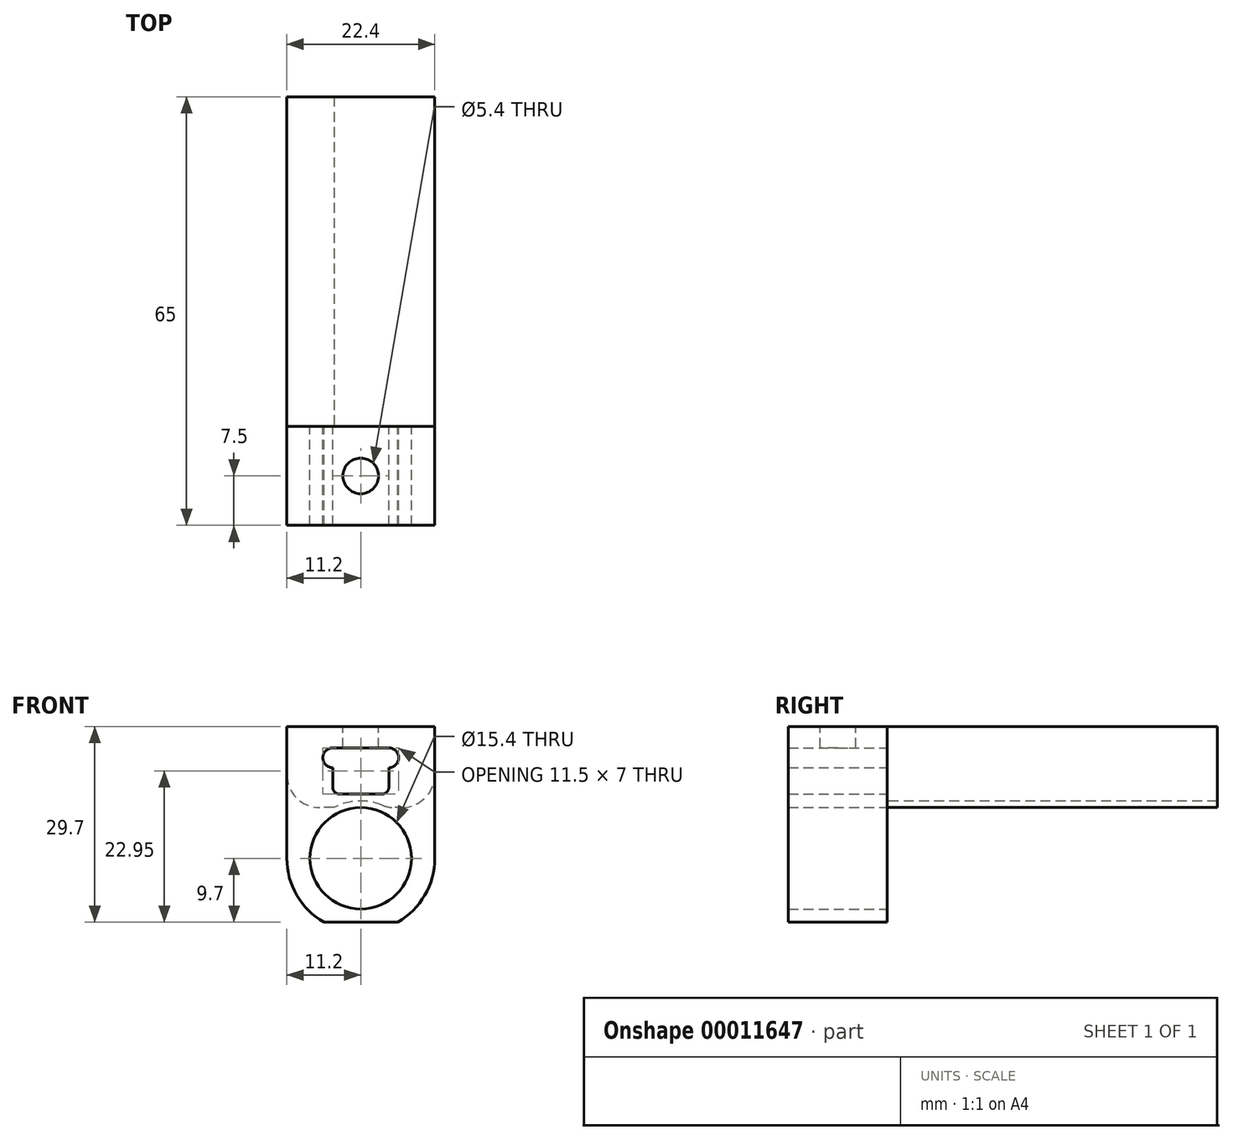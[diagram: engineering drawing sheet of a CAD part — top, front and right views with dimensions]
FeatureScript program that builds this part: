
annotation { "Feature Type Name" : "Feature", "Feature Type Description" : "" }
export const myFeature = defineFeature(function(context is Context, id is Id, definition is map)
    precondition{}
    {
        {
            var Q0;
            Q0=qCreatedBy(makeId("Front.planeOp"),FACE);
            var sketch = newSketch(context, id + "F0", { "sketchPlane" : qUnion([Q0])});
            skCircle(sketch, "E0", {"center": v(0, 0) * mm, "radius": 7.7 * mm});
            skArc(sketch, "E1", {"start": v(-4.18, 10.39) * mm, "mid": v(-11.17, 0.79) * mm, "end": v(-5.6, -9.7) * mm});
            skLineSegment(sketch, "E2", {"start": v(-11.2, 0) * mm, "end": v(-11.2, 20) * mm});
            skLineSegment(sketch, "E3", {"start": v(11.2, 20) * mm, "end": v(11.2, 0) * mm});
            skLineSegment(sketch, "E4", {"start": v(0, 0) * mm, "end": v(0, 20) * mm, "construction": true});
            skLineSegment(sketch, "E5", {"start": v(0, 20) * mm, "end": v(-2.5, 20) * mm});
            skLineSegment(sketch, "E6", {"start": v(-11.2, 20) * mm, "end": v(-2.5, 20) * mm});
            skLineSegment(sketch, "E7", {"start": v(-2.5, 20) * mm, "end": v(-2.5, 16.75) * mm});
            skLineSegment(sketch, "E8", {"start": v(-2.5, 16.75) * mm, "end": v(-4.25, 16.75) * mm});
            skLineSegment(sketch, "E9", {"start": v(-4.25, 16.75) * mm, "end": v(-4.25, 13.75) * mm, "construction": true});
            skLineSegment(sketch, "E10", {"start": v(-4.25, 15.25) * mm, "end": v(-5.75, 15.25) * mm, "construction": true});
            skEllipticalArc(sketch, "E11", {});
            skLineSegment(sketch, "E12", {"start": v(-4.25, 13.75) * mm, "end": v(-4.25, 10.75) * mm});
            skLineSegment(sketch, "E13", {"start": v(-3.25, 9.75) * mm, "end": v(0, 9.75) * mm});
            skPoint(sketch, "E14.visualSharp", {"position": v(-4.25, 9.75) * mm});
            skArc(sketch, "E14.filletArc", {"start": v(-4.25, 10.75) * mm, "mid": v(-3.96, 10.04) * mm, "end": v(-3.25, 9.75) * mm});
            skArc(sketch, "E15.0.MirrorCS", {"start": v(4.25, 10.75) * mm, "mid": v(3.96, 10.04) * mm, "end": v(3.25, 9.75) * mm});
            skEllipticalArc(sketch, "E15.1.MirrorCS", {});
            skLineSegment(sketch, "E15.2.MirrorCS", {"start": v(4.25, 13.75) * mm, "end": v(4.25, 10.75) * mm});
            skPoint(sketch, "E15.3.MirrorP", {"position": v(4.25, 9.75) * mm});
            skLineSegment(sketch, "E15.4.MirrorCS", {"start": v(3.25, 9.75) * mm, "end": v(0, 9.75) * mm});
            skLineSegment(sketch, "E15.5.MirrorCS", {"start": v(11.2, 0) * mm, "end": v(11.2, 20) * mm});
            skLineSegment(sketch, "E15.6.MirrorCS", {"start": v(11.2, 20) * mm, "end": v(2.5, 20) * mm});
            skLineSegment(sketch, "E15.8.MirrorCS", {"start": v(0, 20) * mm, "end": v(2.5, 20) * mm});
            skLineSegment(sketch, "E15.9.MirrorCS", {"start": v(2.5, 16.75) * mm, "end": v(4.25, 16.75) * mm});
            skLineSegment(sketch, "E15.10.MirrorCS", {"start": v(2.5, 20) * mm, "end": v(2.5, 16.75) * mm});
            skPoint(sketch, "E15.11.MirrorCS.end.orphan", {"position": v(5.75, 15.25) * mm});
            skLineSegment(sketch, "E16", {"start": v(-2.5, 16.75) * mm, "end": v(0, 16.75) * mm});
            skLineSegment(sketch, "E17.0.MirrorCS", {"start": v(2.5, 16.75) * mm, "end": v(0, 16.75) * mm});
            skLineSegment(sketch, "E18", {"start": v(0, -7.7) * mm, "end": v(0, -9.7) * mm, "construction": true});
            skLineSegment(sketch, "E19", {"start": v(-5.6, -9.7) * mm, "end": v(5.6, -9.7) * mm});
            skArc(sketch, "E20.trimOffspring", {"start": v(5.6, -9.7) * mm, "mid": v(11.17, 0.79) * mm, "end": v(4.18, 10.39) * mm});
            const initialGuessF0  = {"E11": [-0.00425, 0.01525, 0, 1, 0.0015, 0.0015, 0, 3.141592653589793], "E15.1.MirrorCS": [0.00425, 0.01525, 0, 1, 0.0015, 0.0015, 3.141592653589793, 6.283185307179586]};
            skSetInitialGuess(sketch, initialGuessF0);
            skSolve(sketch);
        }
        {
            var Q0;
            {var subQ1=sQuery(id+"F0.wireOp",EDGE,"E2");Q0=makeQuery(id+"F0.imprint","IMPRINT",FACE,{"disambiguationData":[TD([[makeQuery(id+"F0.imprint","IMPRINT",EDGE,{"derivedFrom":subQ1}),-1.0]])]});}
            var Q1;
            Q1=makeQuery(id+"F0.imprint","IMPRINT",FACE,{"disambiguationData":[TD([[makeQuery(id+"F0.imprint","IMPRINT",EDGE,{"derivedFrom":sQuery(id+"F0.wireOp",EDGE,"E0")}),-1.0]])]});
            var Q2;
            Q2=makeQuery(id+"F0.imprint","IMPRINT",FACE,{"disambiguationData":[TD([[makeQuery(id+"F0.imprint","IMPRINT",EDGE,{"derivedFrom":sQuery(id+"F0.wireOp",EDGE,"E5")}),1.0]])]});
            var Q3;
            Q3=makeQuery(id+"F0.imprint","IMPRINT",FACE,{"disambiguationData":[TD([[makeQuery(id+"F0.imprint","IMPRINT",EDGE,{"derivedFrom":sQuery(id+"F0.wireOp",EDGE,"E15.1.MirrorCS")}),-1.0]])]});
            extrude(context, id + "F1", {"entities" : qUnion([Q0, Q1, Q2, Q3]), "endBound" : BoundingType.SYMMETRIC, "depth" : 15 * mm});
        }
        {
            var Q0;
            Q0=makeQuery(id+"F1.opExtrude","SWEPT_FACE",FACE,{"disambiguationData":[OSD([sQuery(id+"F0.wireOp",EDGE,"E5"),sQuery(id+"F0.wireOp",EDGE,"E6"),sQuery(id+"F0.wireOp",EDGE,"E15.6.MirrorCS"),sQuery(id+"F0.wireOp",EDGE,"E15.8.MirrorCS")])]});
            var sketch = newSketch(context, id + "F2", { "sketchPlane" : qUnion([Q0])});
            skCircle(sketch, "E21", {"center": v(0, 0) * mm, "radius": 2.7 * mm});
            skSolve(sketch);
        }
        {
            var Q0;
            Q0=makeQuery(id+"F2.imprint","IMPRINT",FACE,{"disambiguationData":[TD([[makeQuery(id+"F2.imprint","IMPRINT",EDGE,{"derivedFrom":sQuery(id+"F2.wireOp",EDGE,"E21")}),1.0]])]});
            extrude(context, id + "F3", {"entities" : qUnion([Q0]), "operationType" : NewBodyOperationType.REMOVE, "endBound" : BoundingType.UP_TO_NEXT, "oppositeDirection" : true, "depth" : 25 * mm});
        }
        {
            var Q0;
            Q0=makeQuery(id+"F1.opExtrude","CAP_FACE",FACE,{"disambiguationData":[OSD([sQuery(id+"F0.wireOp",EDGE,"E0"),sQuery(id+"F0.wireOp",EDGE,"E1"),sQuery(id+"F0.wireOp",EDGE,"E2"),sQuery(id+"F0.wireOp",EDGE,"E5"),sQuery(id+"F0.wireOp",EDGE,"E6"),sQuery(id+"F0.wireOp",EDGE,"E8"),sQuery(id+"F0.wireOp",EDGE,"E11"),sQuery(id+"F0.wireOp",EDGE,"E12"),sQuery(id+"F0.wireOp",EDGE,"E13"),sQuery(id+"F0.wireOp",EDGE,"E14.filletArc"),sQuery(id+"F0.wireOp",EDGE,"E15.0.MirrorCS"),sQuery(id+"F0.wireOp",EDGE,"E15.1.MirrorCS"),sQuery(id+"F0.wireOp",EDGE,"E15.2.MirrorCS"),sQuery(id+"F0.wireOp",EDGE,"E15.4.MirrorCS"),sQuery(id+"F0.wireOp",EDGE,"E15.5.MirrorCS"),sQuery(id+"F0.wireOp",EDGE,"E15.6.MirrorCS"),sQuery(id+"F0.wireOp",EDGE,"E15.8.MirrorCS"),sQuery(id+"F0.wireOp",EDGE,"E15.9.MirrorCS"),sQuery(id+"F0.wireOp",EDGE,"E16"),sQuery(id+"F0.wireOp",EDGE,"E17.0.MirrorCS"),sQuery(id+"F0.wireOp",EDGE,"E19"),sQuery(id+"F0.wireOp",EDGE,"E20.trimOffspring")])],"isStart":true});
            var sketch = newSketch(context, id + "F4", { "sketchPlane" : qUnion([Q0])});
            skLineSegment(sketch, "E22", {"start": v(-11.2, 7.7) * mm, "end": v(-4.05, 7.7) * mm});
            skCircle(sketch, "E23", {"center": v(0, 0) * mm, "radius": 8.7 * mm});
            skLineSegment(sketch, "E24.trimOffspring", {"start": v(4.05, 7.7) * mm, "end": v(11.2, 7.7) * mm});
            skSolve(sketch);
        }
        {
            var Q0;
            {var subQ4=sQuery(id+"F4.wireOp",EDGE,"E22");Q0=makeQuery(id+"F4.imprint","IMPRINT",FACE,{"disambiguationData":[TD([[makeQuery(id+"F4.imprint","IMPRINT",EDGE,{"derivedFrom":subQ4}),1.0]])]});}
            var Q1;
            Q1=makeQuery(id+"F4.imprint","IMPRINT",FACE,{"disambiguationData":[TD([[makeQuery(id+"F4.imprint","IMPRINT",EDGE,{"derivedFrom":makeQuery(id+"F1.opExtrude","CAP_EDGE",EDGE,{"disambiguationData":[OSD([sQuery(id+"F0.wireOp",EDGE,"E11")])],"isStart":true})}),-1.0]])]});
            extrude(context, id + "F5", {"entities" : qUnion([Q0, Q1]), "depth" : 50 * mm});
        }
        {
            var Q0;
            Q0=makeQuery(id+"F1.opExtrude","SWEPT_BODY",BODY,{"disambiguationData":[OSD([sQuery(id+"F0.wireOp",EDGE,"E0"),sQuery(id+"F0.wireOp",EDGE,"E1"),sQuery(id+"F0.wireOp",EDGE,"E2"),sQuery(id+"F0.wireOp",EDGE,"E5"),sQuery(id+"F0.wireOp",EDGE,"E6"),sQuery(id+"F0.wireOp",EDGE,"E8"),sQuery(id+"F0.wireOp",EDGE,"E11"),sQuery(id+"F0.wireOp",EDGE,"E12"),sQuery(id+"F0.wireOp",EDGE,"E13"),sQuery(id+"F0.wireOp",EDGE,"E14.filletArc"),sQuery(id+"F0.wireOp",EDGE,"E15.0.MirrorCS"),sQuery(id+"F0.wireOp",EDGE,"E15.1.MirrorCS"),sQuery(id+"F0.wireOp",EDGE,"E15.2.MirrorCS"),sQuery(id+"F0.wireOp",EDGE,"E15.4.MirrorCS"),sQuery(id+"F0.wireOp",EDGE,"E15.5.MirrorCS"),sQuery(id+"F0.wireOp",EDGE,"E15.6.MirrorCS"),sQuery(id+"F0.wireOp",EDGE,"E15.8.MirrorCS"),sQuery(id+"F0.wireOp",EDGE,"E15.9.MirrorCS"),sQuery(id+"F0.wireOp",EDGE,"E16"),sQuery(id+"F0.wireOp",EDGE,"E17.0.MirrorCS"),sQuery(id+"F0.wireOp",EDGE,"E19"),sQuery(id+"F0.wireOp",EDGE,"E20.trimOffspring")])]});
            transform(context, id + "F6", {"entities" : qUnion([Q0]), "transformType" : TransformType.TRANSLATION_3D, "dx" : 0 * mm, "dy" : 58.88 * mm, "dz" : 0 * mm, "makeCopy" : true});
        }
        {
            var Q0;
            Q0=makeQuery(id+"F6.opPattern","COPY",BODY,{"derivedFrom":makeQuery(id+"F1.opExtrude","SWEPT_BODY",BODY,{"disambiguationData":[OSD([sQuery(id+"F0.wireOp",EDGE,"E0"),sQuery(id+"F0.wireOp",EDGE,"E1"),sQuery(id+"F0.wireOp",EDGE,"E2"),sQuery(id+"F0.wireOp",EDGE,"E5"),sQuery(id+"F0.wireOp",EDGE,"E6"),sQuery(id+"F0.wireOp",EDGE,"E8"),sQuery(id+"F0.wireOp",EDGE,"E11"),sQuery(id+"F0.wireOp",EDGE,"E12"),sQuery(id+"F0.wireOp",EDGE,"E13"),sQuery(id+"F0.wireOp",EDGE,"E14.filletArc"),sQuery(id+"F0.wireOp",EDGE,"E15.0.MirrorCS"),sQuery(id+"F0.wireOp",EDGE,"E15.1.MirrorCS"),sQuery(id+"F0.wireOp",EDGE,"E15.2.MirrorCS"),sQuery(id+"F0.wireOp",EDGE,"E15.4.MirrorCS"),sQuery(id+"F0.wireOp",EDGE,"E15.5.MirrorCS"),sQuery(id+"F0.wireOp",EDGE,"E15.6.MirrorCS"),sQuery(id+"F0.wireOp",EDGE,"E15.8.MirrorCS"),sQuery(id+"F0.wireOp",EDGE,"E15.9.MirrorCS"),sQuery(id+"F0.wireOp",EDGE,"E16"),sQuery(id+"F0.wireOp",EDGE,"E17.0.MirrorCS"),sQuery(id+"F0.wireOp",EDGE,"E19"),sQuery(id+"F0.wireOp",EDGE,"E20.trimOffspring")])]}),"instanceName":"1"});
            deleteBodies(context, id + "F7", {"entities" : qUnion([Q0])});
        }
        {
            var Q0;
            Q0=makeQuery(id+"F5.opExtrude","SWEPT_EDGE",EDGE,{"disambiguationData":[OSD([sQuery(id+"F0.wireOp",EDGE,"E2"),sQuery(id+"F4.wireOp",EDGE,"E24.trimOffspring")])]});
            var Q1;
            Q1=makeQuery(id+"F5.opExtrude","SWEPT_EDGE",EDGE,{"disambiguationData":[OSD([sQuery(id+"F0.wireOp",EDGE,"E15.5.MirrorCS"),sQuery(id+"F4.wireOp",EDGE,"E22")])]});
            fillet(context, id + "F8", {"entities" : qUnion([Q0, Q1]), "radius" : 5 * mm, "tangentPropagation" : true, "allowEdgeOverflow" : false});
        }
    });
